# Revit family: SOL2
name_source: partatom
category: Plumbing Fixtures
revit_build: Autodesk Revit 2015 (Build: 20140903_1530(x64)
units: mm (PartAtom-declared; Revit-internal decimal feet)

## types (4) — shared parameters
Aluminum = Aluminum
Glass = Glass
H = 2000 mm  [stored 6.56168 ft]
Manufacturer = SanSwiss
Model = SOL2
Seal = Seal
Type Comments = SOLINO
URL = www.sanswiss.com
zero-valued in all types: Number of elements, Width fixed panel, Width fixed panel 2

## per-type parameters (varying)
| type | L1 | SOL2_half |
| 700x2000 | 700 mm  [stored 2.29659 ft] | SOL2_half : 350 |
| 800x2000 | 800 mm  [stored 2.62467 ft] | SOL2_half : 400 |
| 900x2000 | 900 mm  [stored 2.95276 ft] | SOL2_half : 450 |
| 1000x2000 | 1000 mm  [stored 3.28084 ft] | SOL2_half : 500 |

note: [stored X ft] marks values corroborated as IEEE doubles in the binary element streams (Revit-internal decimal feet)

## geometry (parser evidence)
native form markers: Sweep x11
no freeform markers — native parametric forms only
